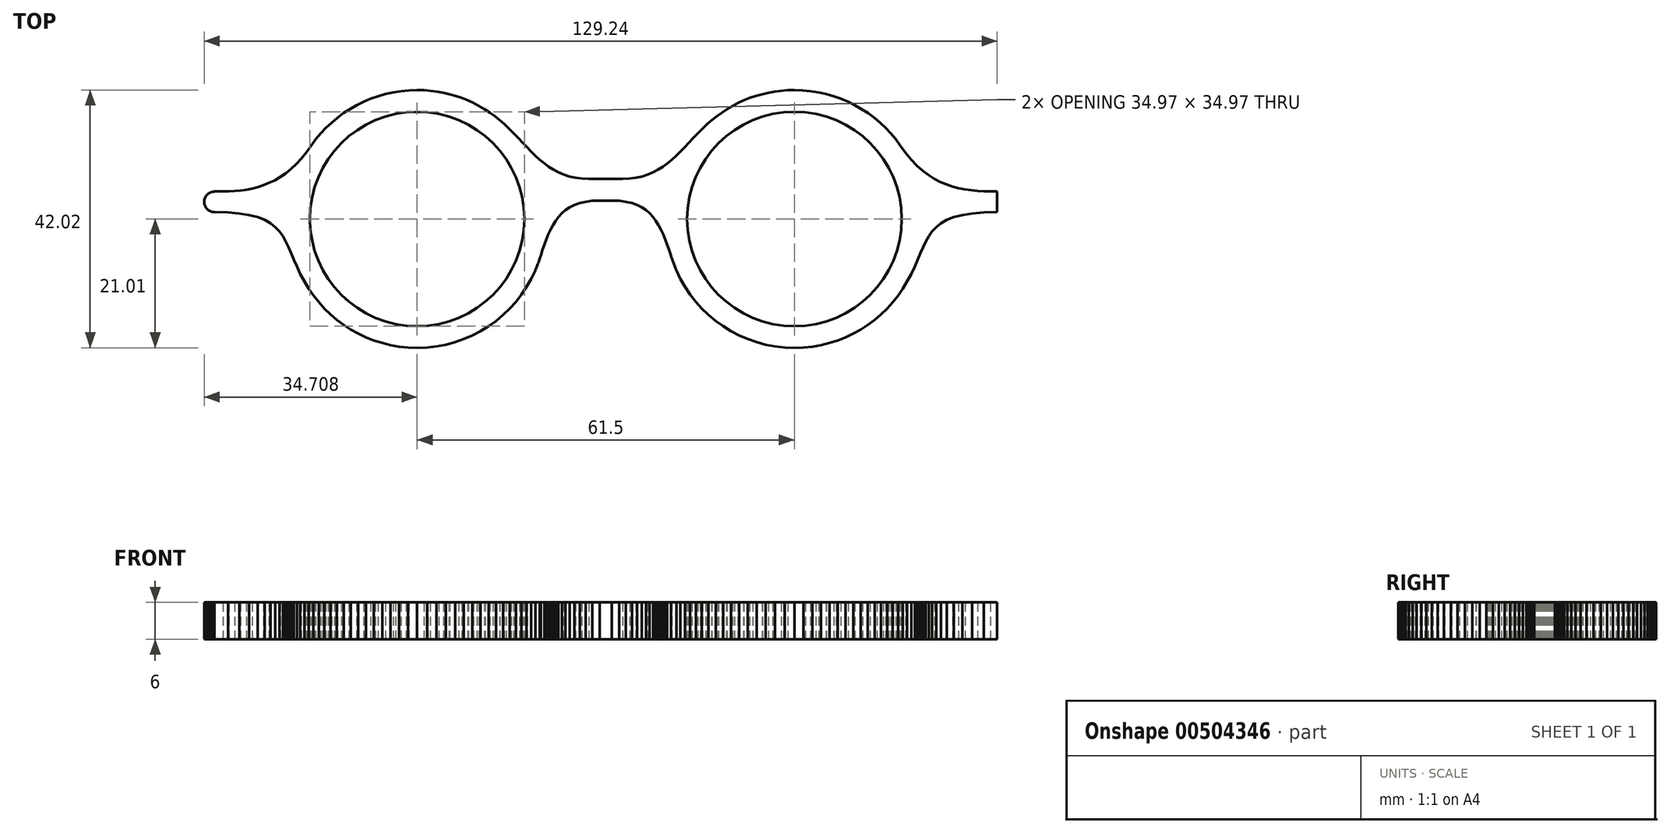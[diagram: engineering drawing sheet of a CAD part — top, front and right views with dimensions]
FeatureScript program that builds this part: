
annotation { "Feature Type Name" : "Feature", "Feature Type Description" : "" }
export const myFeature = defineFeature(function(context is Context, id is Id, definition is map)
    precondition{}
    {
        {
            var Q0;
            Q0=qCreatedBy(makeId("Top.planeOp"),FACE);
            var sketch = newSketch(context, id + "F0", { "sketchPlane" : qUnion([Q0])});
            skLineSegment(sketch, "E0", {"start": v(-47.15, 12) * mm, "end": v(-47.14, 12) * mm});
            skLineSegment(sketch, "E1", {"start": v(-47.14, 12) * mm, "end": v(-47.14, 12.01) * mm});
            skLineSegment(sketch, "E2", {"start": v(-47.14, 12.01) * mm, "end": v(-47.14, 12.01) * mm});
            skLineSegment(sketch, "E3", {"start": v(-47.14, 12.01) * mm, "end": v(-47.14, 12) * mm});
            skLineSegment(sketch, "E4", {"start": v(-47.14, 12) * mm, "end": v(-47.15, 12) * mm});
            skLineSegment(sketch, "E5", {"start": v(-47.15, 12) * mm, "end": v(-47.15, 12) * mm});
            skLineSegment(sketch, "E6", {"start": v(-47.15, 12) * mm, "end": v(-47.16, 12) * mm});
            skLineSegment(sketch, "E7", {"start": v(-47.16, 12) * mm, "end": v(-47.16, 11.99) * mm});
            skLineSegment(sketch, "E8", {"start": v(-47.16, 11.99) * mm, "end": v(-47.16, 11.99) * mm});
            skLineSegment(sketch, "E9", {"start": v(-47.16, 11.99) * mm, "end": v(-47.15, 12) * mm});
            skLineSegment(sketch, "E10", {"start": v(48.83, 11.99) * mm, "end": v(48.83, 12) * mm});
            skLineSegment(sketch, "E11", {"start": v(48.83, 12) * mm, "end": v(48.83, 12) * mm});
            skLineSegment(sketch, "E12", {"start": v(48.83, 12) * mm, "end": v(48.82, 12) * mm});
            skLineSegment(sketch, "E13", {"start": v(48.82, 12) * mm, "end": v(48.82, 12) * mm});
            skLineSegment(sketch, "E14", {"start": v(48.82, 12) * mm, "end": v(48.82, 12.01) * mm});
            skLineSegment(sketch, "E15", {"start": v(48.82, 12.01) * mm, "end": v(48.82, 12.01) * mm});
            skLineSegment(sketch, "E16", {"start": v(48.82, 12.01) * mm, "end": v(48.81, 12.01) * mm});
            skLineSegment(sketch, "E17", {"start": v(48.81, 12.01) * mm, "end": v(48.82, 12.01) * mm});
            skLineSegment(sketch, "E18", {"start": v(48.82, 12.01) * mm, "end": v(48.82, 12) * mm});
            skLineSegment(sketch, "E19", {"start": v(48.82, 12) * mm, "end": v(48.83, 12) * mm});
            skLineSegment(sketch, "E20", {"start": v(48.83, 12) * mm, "end": v(48.83, 11.99) * mm});
            skLineSegment(sketch, "E21", {"start": v(48.83, 11.99) * mm, "end": v(48.83, 11.99) * mm});
            skLineSegment(sketch, "E22", {"start": v(63.55, 4.48) * mm, "end": v(62.5, 4.5) * mm});
            skLineSegment(sketch, "E23", {"start": v(62.5, 4.5) * mm, "end": v(61.45, 4.57) * mm});
            skLineSegment(sketch, "E24", {"start": v(61.45, 4.57) * mm, "end": v(60.41, 4.67) * mm});
            skLineSegment(sketch, "E25", {"start": v(60.41, 4.67) * mm, "end": v(59.38, 4.82) * mm});
            skLineSegment(sketch, "E26", {"start": v(59.38, 4.82) * mm, "end": v(58.36, 5.02) * mm});
            skLineSegment(sketch, "E27", {"start": v(58.36, 5.02) * mm, "end": v(57.35, 5.29) * mm});
            skLineSegment(sketch, "E28", {"start": v(57.35, 5.29) * mm, "end": v(56.35, 5.62) * mm});
            skLineSegment(sketch, "E29", {"start": v(56.35, 5.62) * mm, "end": v(55.36, 6.05) * mm});
            skLineSegment(sketch, "E30", {"start": v(55.36, 6.05) * mm, "end": v(54.38, 6.56) * mm});
            skLineSegment(sketch, "E31", {"start": v(54.38, 6.56) * mm, "end": v(53.42, 7.17) * mm});
            skLineSegment(sketch, "E32", {"start": v(53.42, 7.17) * mm, "end": v(52.47, 7.88) * mm});
            skLineSegment(sketch, "E33", {"start": v(52.47, 7.88) * mm, "end": v(51.54, 8.71) * mm});
            skLineSegment(sketch, "E34", {"start": v(51.54, 8.71) * mm, "end": v(50.62, 9.67) * mm});
            skLineSegment(sketch, "E35", {"start": v(50.62, 9.67) * mm, "end": v(49.72, 10.76) * mm});
            skLineSegment(sketch, "E36", {"start": v(49.72, 10.76) * mm, "end": v(48.83, 11.99) * mm});
            skLineSegment(sketch, "E37", {"start": v(48.83, 11.99) * mm, "end": v(48.1, 12.99) * mm});
            skLineSegment(sketch, "E38", {"start": v(48.1, 12.99) * mm, "end": v(47.3, 13.94) * mm});
            skLineSegment(sketch, "E39", {"start": v(47.3, 13.94) * mm, "end": v(46.44, 14.84) * mm});
            skLineSegment(sketch, "E40", {"start": v(46.44, 14.84) * mm, "end": v(45.54, 15.7) * mm});
            skLineSegment(sketch, "E41", {"start": v(45.54, 15.7) * mm, "end": v(44.59, 16.5) * mm});
            skLineSegment(sketch, "E42", {"start": v(44.59, 16.5) * mm, "end": v(43.59, 17.24) * mm});
            skLineSegment(sketch, "E43", {"start": v(43.59, 17.24) * mm, "end": v(42.54, 17.92) * mm});
            skLineSegment(sketch, "E44", {"start": v(42.54, 17.92) * mm, "end": v(41.46, 18.54) * mm});
            skLineSegment(sketch, "E45", {"start": v(41.46, 18.54) * mm, "end": v(40.34, 19.1) * mm});
            skLineSegment(sketch, "E46", {"start": v(40.34, 19.1) * mm, "end": v(39.18, 19.6) * mm});
            skLineSegment(sketch, "E47", {"start": v(39.18, 19.6) * mm, "end": v(37.98, 20.02) * mm});
            skLineSegment(sketch, "E48", {"start": v(37.98, 20.02) * mm, "end": v(36.76, 20.37) * mm});
            skLineSegment(sketch, "E49", {"start": v(36.76, 20.37) * mm, "end": v(35.5, 20.65) * mm});
            skLineSegment(sketch, "E50", {"start": v(35.5, 20.65) * mm, "end": v(34.22, 20.85) * mm});
            skLineSegment(sketch, "E51", {"start": v(34.22, 20.85) * mm, "end": v(32.92, 20.97) * mm});
            skLineSegment(sketch, "E52", {"start": v(32.92, 20.97) * mm, "end": v(31.59, 21.01) * mm});
            skLineSegment(sketch, "E53", {"start": v(31.59, 21.01) * mm, "end": v(30.5, 20.99) * mm});
            skLineSegment(sketch, "E54", {"start": v(30.5, 20.99) * mm, "end": v(29.42, 20.9) * mm});
            skLineSegment(sketch, "E55", {"start": v(29.42, 20.9) * mm, "end": v(28.36, 20.77) * mm});
            skLineSegment(sketch, "E56", {"start": v(28.36, 20.77) * mm, "end": v(27.32, 20.58) * mm});
            skLineSegment(sketch, "E57", {"start": v(27.32, 20.58) * mm, "end": v(26.3, 20.34) * mm});
            skLineSegment(sketch, "E58", {"start": v(26.3, 20.34) * mm, "end": v(25.3, 20.05) * mm});
            skLineSegment(sketch, "E59", {"start": v(25.3, 20.05) * mm, "end": v(24.31, 19.71) * mm});
            skLineSegment(sketch, "E60", {"start": v(24.31, 19.71) * mm, "end": v(23.35, 19.33) * mm});
            skLineSegment(sketch, "E61", {"start": v(23.35, 19.33) * mm, "end": v(22.41, 18.9) * mm});
            skLineSegment(sketch, "E62", {"start": v(22.41, 18.9) * mm, "end": v(21.5, 18.43) * mm});
            skLineSegment(sketch, "E63", {"start": v(21.5, 18.43) * mm, "end": v(20.62, 17.91) * mm});
            skLineSegment(sketch, "E64", {"start": v(20.62, 17.91) * mm, "end": v(19.76, 17.36) * mm});
            skLineSegment(sketch, "E65", {"start": v(19.76, 17.36) * mm, "end": v(18.93, 16.76) * mm});
            skLineSegment(sketch, "E66", {"start": v(18.93, 16.76) * mm, "end": v(18.13, 16.13) * mm});
            skLineSegment(sketch, "E67", {"start": v(18.13, 16.13) * mm, "end": v(17.37, 15.46) * mm});
            skLineSegment(sketch, "E68", {"start": v(17.37, 15.46) * mm, "end": v(16.63, 14.75) * mm});
            skLineSegment(sketch, "E69", {"start": v(16.63, 14.75) * mm, "end": v(15.85, 13.97) * mm});
            skLineSegment(sketch, "E70", {"start": v(15.85, 13.97) * mm, "end": v(15.1, 13.2) * mm});
            skLineSegment(sketch, "E71", {"start": v(15.1, 13.2) * mm, "end": v(14.38, 12.44) * mm});
            skLineSegment(sketch, "E72", {"start": v(14.38, 12.44) * mm, "end": v(13.67, 11.7) * mm});
            skLineSegment(sketch, "E73", {"start": v(13.67, 11.7) * mm, "end": v(12.97, 10.99) * mm});
            skLineSegment(sketch, "E74", {"start": v(12.97, 10.99) * mm, "end": v(12.28, 10.3) * mm});
            skLineSegment(sketch, "E75", {"start": v(12.28, 10.3) * mm, "end": v(11.58, 9.67) * mm});
            skLineSegment(sketch, "E76", {"start": v(11.58, 9.67) * mm, "end": v(10.86, 9.07) * mm});
            skLineSegment(sketch, "E77", {"start": v(10.86, 9.07) * mm, "end": v(10.12, 8.52) * mm});
            skLineSegment(sketch, "E78", {"start": v(10.12, 8.52) * mm, "end": v(9.35, 8.03) * mm});
            skLineSegment(sketch, "E79", {"start": v(9.35, 8.03) * mm, "end": v(8.54, 7.6) * mm});
            skLineSegment(sketch, "E80", {"start": v(8.54, 7.6) * mm, "end": v(7.68, 7.23) * mm});
            skLineSegment(sketch, "E81", {"start": v(7.68, 7.23) * mm, "end": v(6.77, 6.93) * mm});
            skLineSegment(sketch, "E82", {"start": v(6.77, 6.93) * mm, "end": v(5.78, 6.71) * mm});
            skLineSegment(sketch, "E83", {"start": v(5.78, 6.71) * mm, "end": v(4.73, 6.58) * mm});
            skLineSegment(sketch, "E84", {"start": v(4.73, 6.58) * mm, "end": v(3.6, 6.53) * mm});
            skLineSegment(sketch, "E85", {"start": v(3.6, 6.53) * mm, "end": v(3.25, 6.53) * mm});
            skLineSegment(sketch, "E86", {"start": v(3.25, 6.53) * mm, "end": v(2.9, 6.53) * mm});
            skLineSegment(sketch, "E87", {"start": v(2.9, 6.53) * mm, "end": v(2.56, 6.53) * mm});
            skLineSegment(sketch, "E88", {"start": v(2.56, 6.53) * mm, "end": v(2.21, 6.53) * mm});
            skLineSegment(sketch, "E89", {"start": v(2.21, 6.53) * mm, "end": v(1.87, 6.53) * mm});
            skLineSegment(sketch, "E90", {"start": v(1.87, 6.53) * mm, "end": v(1.53, 6.53) * mm});
            skLineSegment(sketch, "E91", {"start": v(1.53, 6.53) * mm, "end": v(1.18, 6.53) * mm});
            skLineSegment(sketch, "E92", {"start": v(1.18, 6.53) * mm, "end": v(0.84, 6.53) * mm});
            skLineSegment(sketch, "E93", {"start": v(0.84, 6.53) * mm, "end": v(0.5, 6.53) * mm});
            skLineSegment(sketch, "E94", {"start": v(0.5, 6.53) * mm, "end": v(0.15, 6.53) * mm});
            skLineSegment(sketch, "E95", {"start": v(0.15, 6.53) * mm, "end": v(-0.2, 6.53) * mm});
            skLineSegment(sketch, "E96", {"start": v(-0.2, 6.53) * mm, "end": v(-0.54, 6.53) * mm});
            skLineSegment(sketch, "E97", {"start": v(-0.54, 6.53) * mm, "end": v(-0.88, 6.53) * mm});
            skLineSegment(sketch, "E98", {"start": v(-0.88, 6.53) * mm, "end": v(-1.23, 6.53) * mm});
            skLineSegment(sketch, "E99", {"start": v(-1.23, 6.53) * mm, "end": v(-1.57, 6.53) * mm});
            skLineSegment(sketch, "E100", {"start": v(-1.57, 6.53) * mm, "end": v(-1.92, 6.53) * mm});
            skLineSegment(sketch, "E101", {"start": v(-1.92, 6.53) * mm, "end": v(-3.05, 6.58) * mm});
            skLineSegment(sketch, "E102", {"start": v(-3.05, 6.58) * mm, "end": v(-4.1, 6.71) * mm});
            skLineSegment(sketch, "E103", {"start": v(-4.1, 6.71) * mm, "end": v(-5.1, 6.93) * mm});
            skLineSegment(sketch, "E104", {"start": v(-5.1, 6.93) * mm, "end": v(-6, 7.23) * mm});
            skLineSegment(sketch, "E105", {"start": v(-6, 7.23) * mm, "end": v(-6.87, 7.6) * mm});
            skLineSegment(sketch, "E106", {"start": v(-6.87, 7.6) * mm, "end": v(-7.68, 8.03) * mm});
            skLineSegment(sketch, "E107", {"start": v(-7.68, 8.03) * mm, "end": v(-8.45, 8.52) * mm});
            skLineSegment(sketch, "E108", {"start": v(-8.45, 8.52) * mm, "end": v(-9.19, 9.07) * mm});
            skLineSegment(sketch, "E109", {"start": v(-9.19, 9.07) * mm, "end": v(-9.9, 9.67) * mm});
            skLineSegment(sketch, "E110", {"start": v(-9.9, 9.67) * mm, "end": v(-10.6, 10.3) * mm});
            skLineSegment(sketch, "E111", {"start": v(-10.6, 10.3) * mm, "end": v(-11.3, 10.99) * mm});
            skLineSegment(sketch, "E112", {"start": v(-11.3, 10.99) * mm, "end": v(-12, 11.7) * mm});
            skLineSegment(sketch, "E113", {"start": v(-12, 11.7) * mm, "end": v(-12.7, 12.44) * mm});
            skLineSegment(sketch, "E114", {"start": v(-12.7, 12.44) * mm, "end": v(-13.42, 13.2) * mm});
            skLineSegment(sketch, "E115", {"start": v(-13.42, 13.2) * mm, "end": v(-14.17, 13.97) * mm});
            skLineSegment(sketch, "E116", {"start": v(-14.17, 13.97) * mm, "end": v(-14.96, 14.75) * mm});
            skLineSegment(sketch, "E117", {"start": v(-14.96, 14.75) * mm, "end": v(-15.7, 15.46) * mm});
            skLineSegment(sketch, "E118", {"start": v(-15.7, 15.46) * mm, "end": v(-16.46, 16.13) * mm});
            skLineSegment(sketch, "E119", {"start": v(-16.46, 16.13) * mm, "end": v(-17.26, 16.76) * mm});
            skLineSegment(sketch, "E120", {"start": v(-17.26, 16.76) * mm, "end": v(-18.08, 17.36) * mm});
            skLineSegment(sketch, "E121", {"start": v(-18.08, 17.36) * mm, "end": v(-18.94, 17.91) * mm});
            skLineSegment(sketch, "E122", {"start": v(-18.94, 17.91) * mm, "end": v(-19.83, 18.43) * mm});
            skLineSegment(sketch, "E123", {"start": v(-19.83, 18.43) * mm, "end": v(-20.74, 18.9) * mm});
            skLineSegment(sketch, "E124", {"start": v(-20.74, 18.9) * mm, "end": v(-21.67, 19.33) * mm});
            skLineSegment(sketch, "E125", {"start": v(-21.67, 19.33) * mm, "end": v(-22.64, 19.71) * mm});
            skLineSegment(sketch, "E126", {"start": v(-22.64, 19.71) * mm, "end": v(-23.62, 20.05) * mm});
            skLineSegment(sketch, "E127", {"start": v(-23.62, 20.05) * mm, "end": v(-24.62, 20.34) * mm});
            skLineSegment(sketch, "E128", {"start": v(-24.62, 20.34) * mm, "end": v(-25.65, 20.58) * mm});
            skLineSegment(sketch, "E129", {"start": v(-25.65, 20.58) * mm, "end": v(-26.69, 20.77) * mm});
            skLineSegment(sketch, "E130", {"start": v(-26.69, 20.77) * mm, "end": v(-27.75, 20.9) * mm});
            skLineSegment(sketch, "E131", {"start": v(-27.75, 20.9) * mm, "end": v(-28.82, 20.99) * mm});
            skLineSegment(sketch, "E132", {"start": v(-28.82, 20.99) * mm, "end": v(-29.91, 21.01) * mm});
            skLineSegment(sketch, "E133", {"start": v(-29.91, 21.01) * mm, "end": v(-31.24, 20.97) * mm});
            skLineSegment(sketch, "E134", {"start": v(-31.24, 20.97) * mm, "end": v(-32.55, 20.85) * mm});
            skLineSegment(sketch, "E135", {"start": v(-32.55, 20.85) * mm, "end": v(-33.83, 20.65) * mm});
            skLineSegment(sketch, "E136", {"start": v(-33.83, 20.65) * mm, "end": v(-35.08, 20.37) * mm});
            skLineSegment(sketch, "E137", {"start": v(-35.08, 20.37) * mm, "end": v(-36.3, 20.02) * mm});
            skLineSegment(sketch, "E138", {"start": v(-36.3, 20.02) * mm, "end": v(-37.5, 19.6) * mm});
            skLineSegment(sketch, "E139", {"start": v(-37.5, 19.6) * mm, "end": v(-38.66, 19.1) * mm});
            skLineSegment(sketch, "E140", {"start": v(-38.66, 19.1) * mm, "end": v(-39.78, 18.54) * mm});
            skLineSegment(sketch, "E141", {"start": v(-39.78, 18.54) * mm, "end": v(-40.87, 17.92) * mm});
            skLineSegment(sketch, "E142", {"start": v(-40.87, 17.92) * mm, "end": v(-41.91, 17.24) * mm});
            skLineSegment(sketch, "E143", {"start": v(-41.91, 17.24) * mm, "end": v(-42.91, 16.5) * mm});
            skLineSegment(sketch, "E144", {"start": v(-42.91, 16.5) * mm, "end": v(-43.86, 15.7) * mm});
            skLineSegment(sketch, "E145", {"start": v(-43.86, 15.7) * mm, "end": v(-44.77, 14.84) * mm});
            skLineSegment(sketch, "E146", {"start": v(-44.77, 14.84) * mm, "end": v(-45.62, 13.94) * mm});
            skLineSegment(sketch, "E147", {"start": v(-45.62, 13.94) * mm, "end": v(-46.42, 12.99) * mm});
            skLineSegment(sketch, "E148", {"start": v(-46.42, 12.99) * mm, "end": v(-47.16, 11.99) * mm});
            skLineSegment(sketch, "E149", {"start": v(-47.16, 11.99) * mm, "end": v(-47.97, 10.85) * mm});
            skLineSegment(sketch, "E150", {"start": v(-47.97, 10.85) * mm, "end": v(-48.8, 9.84) * mm});
            skLineSegment(sketch, "E151", {"start": v(-48.8, 9.84) * mm, "end": v(-49.64, 8.93) * mm});
            skLineSegment(sketch, "E152", {"start": v(-49.64, 8.93) * mm, "end": v(-50.5, 8.14) * mm});
            skLineSegment(sketch, "E153", {"start": v(-50.5, 8.14) * mm, "end": v(-51.36, 7.44) * mm});
            skLineSegment(sketch, "E154", {"start": v(-51.36, 7.44) * mm, "end": v(-52.24, 6.83) * mm});
            skLineSegment(sketch, "E155", {"start": v(-52.24, 6.83) * mm, "end": v(-53.13, 6.31) * mm});
            skLineSegment(sketch, "E156", {"start": v(-53.13, 6.31) * mm, "end": v(-54.03, 5.87) * mm});
            skLineSegment(sketch, "E157", {"start": v(-54.03, 5.87) * mm, "end": v(-54.95, 5.5) * mm});
            skLineSegment(sketch, "E158", {"start": v(-54.95, 5.5) * mm, "end": v(-55.87, 5.2) * mm});
            skLineSegment(sketch, "E159", {"start": v(-55.87, 5.2) * mm, "end": v(-56.8, 4.97) * mm});
            skLineSegment(sketch, "E160", {"start": v(-56.8, 4.97) * mm, "end": v(-57.73, 4.79) * mm});
            skLineSegment(sketch, "E161", {"start": v(-57.73, 4.79) * mm, "end": v(-58.68, 4.65) * mm});
            skLineSegment(sketch, "E162", {"start": v(-58.68, 4.65) * mm, "end": v(-59.63, 4.56) * mm});
            skLineSegment(sketch, "E163", {"start": v(-59.63, 4.56) * mm, "end": v(-60.58, 4.5) * mm});
            skLineSegment(sketch, "E164", {"start": v(-60.58, 4.5) * mm, "end": v(-61.54, 4.48) * mm});
            skLineSegment(sketch, "E165", {"start": v(-61.54, 4.48) * mm, "end": v(-61.63, 4.48) * mm});
            skLineSegment(sketch, "E166", {"start": v(-61.63, 4.48) * mm, "end": v(-61.72, 4.48) * mm});
            skLineSegment(sketch, "E167", {"start": v(-61.72, 4.48) * mm, "end": v(-61.8, 4.48) * mm});
            skLineSegment(sketch, "E168", {"start": v(-61.8, 4.48) * mm, "end": v(-61.9, 4.48) * mm});
            skLineSegment(sketch, "E169", {"start": v(-61.9, 4.48) * mm, "end": v(-61.98, 4.48) * mm});
            skLineSegment(sketch, "E170", {"start": v(-61.98, 4.48) * mm, "end": v(-62.07, 4.48) * mm});
            skLineSegment(sketch, "E171", {"start": v(-62.07, 4.48) * mm, "end": v(-62.16, 4.48) * mm});
            skLineSegment(sketch, "E172", {"start": v(-62.16, 4.48) * mm, "end": v(-62.24, 4.47) * mm});
            skLineSegment(sketch, "E173", {"start": v(-62.24, 4.47) * mm, "end": v(-62.33, 4.47) * mm});
            skLineSegment(sketch, "E174", {"start": v(-62.33, 4.47) * mm, "end": v(-62.42, 4.47) * mm});
            skLineSegment(sketch, "E175", {"start": v(-62.42, 4.47) * mm, "end": v(-62.5, 4.47) * mm});
            skLineSegment(sketch, "E176", {"start": v(-62.5, 4.47) * mm, "end": v(-62.6, 4.47) * mm});
            skLineSegment(sketch, "E177", {"start": v(-62.6, 4.47) * mm, "end": v(-62.68, 4.47) * mm});
            skLineSegment(sketch, "E178", {"start": v(-62.68, 4.47) * mm, "end": v(-62.77, 4.47) * mm});
            skLineSegment(sketch, "E179", {"start": v(-62.77, 4.47) * mm, "end": v(-62.85, 4.47) * mm});
            skLineSegment(sketch, "E180", {"start": v(-62.85, 4.47) * mm, "end": v(-62.94, 4.47) * mm});
            skLineSegment(sketch, "E181", {"start": v(-62.94, 4.47) * mm, "end": v(-62.94, 4.47) * mm});
            skLineSegment(sketch, "E182", {"start": v(-62.94, 4.47) * mm, "end": v(-63.11, 4.46) * mm});
            skLineSegment(sketch, "E183", {"start": v(-63.11, 4.46) * mm, "end": v(-63.28, 4.44) * mm});
            skLineSegment(sketch, "E184", {"start": v(-63.28, 4.44) * mm, "end": v(-63.44, 4.4) * mm});
            skLineSegment(sketch, "E185", {"start": v(-63.44, 4.4) * mm, "end": v(-63.6, 4.34) * mm});
            skLineSegment(sketch, "E186", {"start": v(-63.6, 4.34) * mm, "end": v(-63.74, 4.27) * mm});
            skLineSegment(sketch, "E187", {"start": v(-63.74, 4.27) * mm, "end": v(-63.88, 4.18) * mm});
            skLineSegment(sketch, "E188", {"start": v(-63.88, 4.18) * mm, "end": v(-64, 4.09) * mm});
            skLineSegment(sketch, "E189", {"start": v(-64, 4.09) * mm, "end": v(-64.12, 3.98) * mm});
            skLineSegment(sketch, "E190", {"start": v(-64.12, 3.98) * mm, "end": v(-64.23, 3.86) * mm});
            skLineSegment(sketch, "E191", {"start": v(-64.23, 3.86) * mm, "end": v(-64.33, 3.73) * mm});
            skLineSegment(sketch, "E192", {"start": v(-64.33, 3.73) * mm, "end": v(-64.41, 3.6) * mm});
            skLineSegment(sketch, "E193", {"start": v(-64.41, 3.6) * mm, "end": v(-64.48, 3.45) * mm});
            skLineSegment(sketch, "E194", {"start": v(-64.48, 3.45) * mm, "end": v(-64.54, 3.3) * mm});
            skLineSegment(sketch, "E195", {"start": v(-64.54, 3.3) * mm, "end": v(-64.58, 3.13) * mm});
            skLineSegment(sketch, "E196", {"start": v(-64.58, 3.13) * mm, "end": v(-64.6, 2.97) * mm});
            skLineSegment(sketch, "E197", {"start": v(-64.6, 2.97) * mm, "end": v(-64.62, 2.8) * mm});
            skLineSegment(sketch, "E198", {"start": v(-64.62, 2.8) * mm, "end": v(-64.6, 2.62) * mm});
            skLineSegment(sketch, "E199", {"start": v(-64.6, 2.62) * mm, "end": v(-64.58, 2.46) * mm});
            skLineSegment(sketch, "E200", {"start": v(-64.58, 2.46) * mm, "end": v(-64.54, 2.3) * mm});
            skLineSegment(sketch, "E201", {"start": v(-64.54, 2.3) * mm, "end": v(-64.48, 2.14) * mm});
            skLineSegment(sketch, "E202", {"start": v(-64.48, 2.14) * mm, "end": v(-64.41, 2) * mm});
            skLineSegment(sketch, "E203", {"start": v(-64.41, 2) * mm, "end": v(-64.33, 1.86) * mm});
            skLineSegment(sketch, "E204", {"start": v(-64.33, 1.86) * mm, "end": v(-64.23, 1.73) * mm});
            skLineSegment(sketch, "E205", {"start": v(-64.23, 1.73) * mm, "end": v(-64.12, 1.6) * mm});
            skLineSegment(sketch, "E206", {"start": v(-64.12, 1.6) * mm, "end": v(-64, 1.5) * mm});
            skLineSegment(sketch, "E207", {"start": v(-64, 1.5) * mm, "end": v(-63.88, 1.4) * mm});
            skLineSegment(sketch, "E208", {"start": v(-63.88, 1.4) * mm, "end": v(-63.74, 1.32) * mm});
            skLineSegment(sketch, "E209", {"start": v(-63.74, 1.32) * mm, "end": v(-63.6, 1.25) * mm});
            skLineSegment(sketch, "E210", {"start": v(-63.6, 1.25) * mm, "end": v(-63.44, 1.2) * mm});
            skLineSegment(sketch, "E211", {"start": v(-63.44, 1.2) * mm, "end": v(-63.28, 1.15) * mm});
            skLineSegment(sketch, "E212", {"start": v(-63.28, 1.15) * mm, "end": v(-63.11, 1.13) * mm});
            skLineSegment(sketch, "E213", {"start": v(-63.11, 1.13) * mm, "end": v(-62.94, 1.12) * mm});
            skLineSegment(sketch, "E214", {"start": v(-62.94, 1.12) * mm, "end": v(-62.94, 1.12) * mm});
            skLineSegment(sketch, "E215", {"start": v(-62.94, 1.12) * mm, "end": v(-60.76, 1.06) * mm});
            skLineSegment(sketch, "E216", {"start": v(-60.76, 1.06) * mm, "end": v(-58.88, 0.9) * mm});
            skLineSegment(sketch, "E217", {"start": v(-58.88, 0.9) * mm, "end": v(-57.28, 0.65) * mm});
            skLineSegment(sketch, "E218", {"start": v(-57.28, 0.65) * mm, "end": v(-55.92, 0.29) * mm});
            skLineSegment(sketch, "E219", {"start": v(-55.92, 0.29) * mm, "end": v(-54.78, -0.16) * mm});
            skLineSegment(sketch, "E220", {"start": v(-54.78, -0.16) * mm, "end": v(-53.82, -0.7) * mm});
            skLineSegment(sketch, "E221", {"start": v(-53.82, -0.7) * mm, "end": v(-53.03, -1.33) * mm});
            skLineSegment(sketch, "E222", {"start": v(-53.03, -1.33) * mm, "end": v(-52.37, -2.04) * mm});
            skLineSegment(sketch, "E223", {"start": v(-52.37, -2.04) * mm, "end": v(-51.8, -2.82) * mm});
            skLineSegment(sketch, "E224", {"start": v(-51.8, -2.82) * mm, "end": v(-51.32, -3.68) * mm});
            skLineSegment(sketch, "E225", {"start": v(-51.32, -3.68) * mm, "end": v(-50.88, -4.6) * mm});
            skLineSegment(sketch, "E226", {"start": v(-50.88, -4.6) * mm, "end": v(-50.45, -5.6) * mm});
            skLineSegment(sketch, "E227", {"start": v(-50.45, -5.6) * mm, "end": v(-50, -6.66) * mm});
            skLineSegment(sketch, "E228", {"start": v(-50, -6.66) * mm, "end": v(-49.52, -7.77) * mm});
            skLineSegment(sketch, "E229", {"start": v(-49.52, -7.77) * mm, "end": v(-48.96, -8.94) * mm});
            skLineSegment(sketch, "E230", {"start": v(-48.96, -8.94) * mm, "end": v(-48.3, -10.15) * mm});
            skLineSegment(sketch, "E231", {"start": v(-48.3, -10.15) * mm, "end": v(-47.6, -11.34) * mm});
            skLineSegment(sketch, "E232", {"start": v(-47.6, -11.34) * mm, "end": v(-46.8, -12.48) * mm});
            skLineSegment(sketch, "E233", {"start": v(-46.8, -12.48) * mm, "end": v(-45.95, -13.56) * mm});
            skLineSegment(sketch, "E234", {"start": v(-45.95, -13.56) * mm, "end": v(-45.03, -14.58) * mm});
            skLineSegment(sketch, "E235", {"start": v(-45.03, -14.58) * mm, "end": v(-44.04, -15.54) * mm});
            skLineSegment(sketch, "E236", {"start": v(-44.04, -15.54) * mm, "end": v(-43, -16.43) * mm});
            skLineSegment(sketch, "E237", {"start": v(-43, -16.43) * mm, "end": v(-41.89, -17.26) * mm});
            skLineSegment(sketch, "E238", {"start": v(-41.89, -17.26) * mm, "end": v(-40.73, -18) * mm});
            skLineSegment(sketch, "E239", {"start": v(-40.73, -18) * mm, "end": v(-39.52, -18.69) * mm});
            skLineSegment(sketch, "E240", {"start": v(-39.52, -18.69) * mm, "end": v(-38.26, -19.28) * mm});
            skLineSegment(sketch, "E241", {"start": v(-38.26, -19.28) * mm, "end": v(-36.96, -19.8) * mm});
            skLineSegment(sketch, "E242", {"start": v(-36.96, -19.8) * mm, "end": v(-35.62, -20.23) * mm});
            skLineSegment(sketch, "E243", {"start": v(-35.62, -20.23) * mm, "end": v(-34.24, -20.57) * mm});
            skLineSegment(sketch, "E244", {"start": v(-34.24, -20.57) * mm, "end": v(-32.83, -20.81) * mm});
            skLineSegment(sketch, "E245", {"start": v(-32.83, -20.81) * mm, "end": v(-31.38, -20.96) * mm});
            skLineSegment(sketch, "E246", {"start": v(-31.38, -20.96) * mm, "end": v(-29.91, -21.01) * mm});
            skLineSegment(sketch, "E247", {"start": v(-29.91, -21.01) * mm, "end": v(-28.31, -20.95) * mm});
            skLineSegment(sketch, "E248", {"start": v(-28.31, -20.95) * mm, "end": v(-26.75, -20.78) * mm});
            skLineSegment(sketch, "E249", {"start": v(-26.75, -20.78) * mm, "end": v(-25.22, -20.49) * mm});
            skLineSegment(sketch, "E250", {"start": v(-25.22, -20.49) * mm, "end": v(-23.73, -20.09) * mm});
            skLineSegment(sketch, "E251", {"start": v(-23.73, -20.09) * mm, "end": v(-22.3, -19.58) * mm});
            skLineSegment(sketch, "E252", {"start": v(-22.3, -19.58) * mm, "end": v(-20.9, -18.98) * mm});
            skLineSegment(sketch, "E253", {"start": v(-20.9, -18.98) * mm, "end": v(-19.56, -18.28) * mm});
            skLineSegment(sketch, "E254", {"start": v(-19.56, -18.28) * mm, "end": v(-18.28, -17.5) * mm});
            skLineSegment(sketch, "E255", {"start": v(-18.28, -17.5) * mm, "end": v(-17.06, -16.61) * mm});
            skLineSegment(sketch, "E256", {"start": v(-17.06, -16.61) * mm, "end": v(-15.91, -15.65) * mm});
            skLineSegment(sketch, "E257", {"start": v(-15.91, -15.65) * mm, "end": v(-14.83, -14.62) * mm});
            skLineSegment(sketch, "E258", {"start": v(-14.83, -14.62) * mm, "end": v(-13.83, -13.5) * mm});
            skLineSegment(sketch, "E259", {"start": v(-13.83, -13.5) * mm, "end": v(-12.9, -12.32) * mm});
            skLineSegment(sketch, "E260", {"start": v(-12.9, -12.32) * mm, "end": v(-12.07, -11.08) * mm});
            skLineSegment(sketch, "E261", {"start": v(-12.07, -11.08) * mm, "end": v(-11.32, -9.77) * mm});
            skLineSegment(sketch, "E262", {"start": v(-11.32, -9.77) * mm, "end": v(-10.66, -8.4) * mm});
            skLineSegment(sketch, "E263", {"start": v(-10.66, -8.4) * mm, "end": v(-10.65, -8.4) * mm});
            skLineSegment(sketch, "E264", {"start": v(-10.65, -8.4) * mm, "end": v(-10.63, -8.34) * mm});
            skLineSegment(sketch, "E265", {"start": v(-10.63, -8.34) * mm, "end": v(-10.6, -8.25) * mm});
            skLineSegment(sketch, "E266", {"start": v(-10.6, -8.25) * mm, "end": v(-10.55, -8.14) * mm});
            skLineSegment(sketch, "E267", {"start": v(-10.55, -8.14) * mm, "end": v(-10.5, -8) * mm});
            skLineSegment(sketch, "E268", {"start": v(-10.5, -8) * mm, "end": v(-10.44, -7.85) * mm});
            skLineSegment(sketch, "E269", {"start": v(-10.44, -7.85) * mm, "end": v(-10.37, -7.68) * mm});
            skLineSegment(sketch, "E270", {"start": v(-10.37, -7.68) * mm, "end": v(-10.3, -7.5) * mm});
            skLineSegment(sketch, "E271", {"start": v(-10.3, -7.5) * mm, "end": v(-10.23, -7.3) * mm});
            skLineSegment(sketch, "E272", {"start": v(-10.23, -7.3) * mm, "end": v(-10.15, -7.1) * mm});
            skLineSegment(sketch, "E273", {"start": v(-10.15, -7.1) * mm, "end": v(-10.08, -6.89) * mm});
            skLineSegment(sketch, "E274", {"start": v(-10.08, -6.89) * mm, "end": v(-10, -6.68) * mm});
            skLineSegment(sketch, "E275", {"start": v(-10, -6.68) * mm, "end": v(-9.94, -6.49) * mm});
            skLineSegment(sketch, "E276", {"start": v(-9.94, -6.49) * mm, "end": v(-9.87, -6.3) * mm});
            skLineSegment(sketch, "E277", {"start": v(-9.87, -6.3) * mm, "end": v(-9.81, -6.12) * mm});
            skLineSegment(sketch, "E278", {"start": v(-9.81, -6.12) * mm, "end": v(-9.76, -5.95) * mm});
            skLineSegment(sketch, "E279", {"start": v(-9.76, -5.95) * mm, "end": v(-9.46, -5.05) * mm});
            skLineSegment(sketch, "E280", {"start": v(-9.46, -5.05) * mm, "end": v(-9.15, -4.18) * mm});
            skLineSegment(sketch, "E281", {"start": v(-9.15, -4.18) * mm, "end": v(-8.84, -3.33) * mm});
            skLineSegment(sketch, "E282", {"start": v(-8.84, -3.33) * mm, "end": v(-8.51, -2.51) * mm});
            skLineSegment(sketch, "E283", {"start": v(-8.51, -2.51) * mm, "end": v(-8.16, -1.73) * mm});
            skLineSegment(sketch, "E284", {"start": v(-8.16, -1.73) * mm, "end": v(-7.77, -1) * mm});
            skLineSegment(sketch, "E285", {"start": v(-7.77, -1) * mm, "end": v(-7.35, -0.3) * mm});
            skLineSegment(sketch, "E286", {"start": v(-7.35, -0.3) * mm, "end": v(-6.87, 0.34) * mm});
            skLineSegment(sketch, "E287", {"start": v(-6.87, 0.34) * mm, "end": v(-6.33, 0.93) * mm});
            skLineSegment(sketch, "E288", {"start": v(-6.33, 0.93) * mm, "end": v(-5.73, 1.45) * mm});
            skLineSegment(sketch, "E289", {"start": v(-5.73, 1.45) * mm, "end": v(-5.04, 1.9) * mm});
            skLineSegment(sketch, "E290", {"start": v(-5.04, 1.9) * mm, "end": v(-4.28, 2.29) * mm});
            skLineSegment(sketch, "E291", {"start": v(-4.28, 2.29) * mm, "end": v(-3.41, 2.6) * mm});
            skLineSegment(sketch, "E292", {"start": v(-3.41, 2.6) * mm, "end": v(-2.44, 2.82) * mm});
            skLineSegment(sketch, "E293", {"start": v(-2.44, 2.82) * mm, "end": v(-1.36, 2.96) * mm});
            skLineSegment(sketch, "E294", {"start": v(-1.36, 2.96) * mm, "end": v(-0.16, 3) * mm});
            skLineSegment(sketch, "E295", {"start": v(-0.16, 3) * mm, "end": v(-0.04, 3) * mm});
            skLineSegment(sketch, "E296", {"start": v(-0.04, 3) * mm, "end": v(0.09, 3) * mm});
            skLineSegment(sketch, "E297", {"start": v(0.09, 3) * mm, "end": v(0.21, 3) * mm});
            skLineSegment(sketch, "E298", {"start": v(0.21, 3) * mm, "end": v(0.34, 3) * mm});
            skLineSegment(sketch, "E299", {"start": v(0.34, 3) * mm, "end": v(0.46, 3) * mm});
            skLineSegment(sketch, "E300", {"start": v(0.46, 3) * mm, "end": v(0.59, 3) * mm});
            skLineSegment(sketch, "E301", {"start": v(0.59, 3) * mm, "end": v(0.71, 3) * mm});
            skLineSegment(sketch, "E302", {"start": v(0.71, 3) * mm, "end": v(0.84, 3) * mm});
            skLineSegment(sketch, "E303", {"start": v(0.84, 3) * mm, "end": v(0.96, 3) * mm});
            skLineSegment(sketch, "E304", {"start": v(0.96, 3) * mm, "end": v(1.09, 3) * mm});
            skLineSegment(sketch, "E305", {"start": v(1.09, 3) * mm, "end": v(1.21, 3) * mm});
            skLineSegment(sketch, "E306", {"start": v(1.21, 3) * mm, "end": v(1.34, 3) * mm});
            skLineSegment(sketch, "E307", {"start": v(1.34, 3) * mm, "end": v(1.46, 3) * mm});
            skLineSegment(sketch, "E308", {"start": v(1.46, 3) * mm, "end": v(1.59, 3) * mm});
            skLineSegment(sketch, "E309", {"start": v(1.59, 3) * mm, "end": v(1.71, 3) * mm});
            skLineSegment(sketch, "E310", {"start": v(1.71, 3) * mm, "end": v(1.84, 3) * mm});
            skLineSegment(sketch, "E311", {"start": v(1.84, 3) * mm, "end": v(3.04, 2.96) * mm});
            skLineSegment(sketch, "E312", {"start": v(3.04, 2.96) * mm, "end": v(4.12, 2.82) * mm});
            skLineSegment(sketch, "E313", {"start": v(4.12, 2.82) * mm, "end": v(5.09, 2.6) * mm});
            skLineSegment(sketch, "E314", {"start": v(5.09, 2.6) * mm, "end": v(5.95, 2.29) * mm});
            skLineSegment(sketch, "E315", {"start": v(5.95, 2.29) * mm, "end": v(6.72, 1.9) * mm});
            skLineSegment(sketch, "E316", {"start": v(6.72, 1.9) * mm, "end": v(7.4, 1.45) * mm});
            skLineSegment(sketch, "E317", {"start": v(7.4, 1.45) * mm, "end": v(8, 0.93) * mm});
            skLineSegment(sketch, "E318", {"start": v(8, 0.93) * mm, "end": v(8.55, 0.34) * mm});
            skLineSegment(sketch, "E319", {"start": v(8.55, 0.34) * mm, "end": v(9.02, -0.3) * mm});
            skLineSegment(sketch, "E320", {"start": v(9.02, -0.3) * mm, "end": v(9.45, -1) * mm});
            skLineSegment(sketch, "E321", {"start": v(9.45, -1) * mm, "end": v(9.83, -1.73) * mm});
            skLineSegment(sketch, "E322", {"start": v(9.83, -1.73) * mm, "end": v(10.19, -2.51) * mm});
            skLineSegment(sketch, "E323", {"start": v(10.19, -2.51) * mm, "end": v(10.51, -3.33) * mm});
            skLineSegment(sketch, "E324", {"start": v(10.51, -3.33) * mm, "end": v(10.82, -4.18) * mm});
            skLineSegment(sketch, "E325", {"start": v(10.82, -4.18) * mm, "end": v(11.13, -5.05) * mm});
            skLineSegment(sketch, "E326", {"start": v(11.13, -5.05) * mm, "end": v(11.44, -5.95) * mm});
            skLineSegment(sketch, "E327", {"start": v(11.44, -5.95) * mm, "end": v(11.5, -6.1) * mm});
            skLineSegment(sketch, "E328", {"start": v(11.5, -6.1) * mm, "end": v(11.55, -6.26) * mm});
            skLineSegment(sketch, "E329", {"start": v(11.55, -6.26) * mm, "end": v(11.6, -6.41) * mm});
            skLineSegment(sketch, "E330", {"start": v(11.6, -6.41) * mm, "end": v(11.66, -6.57) * mm});
            skLineSegment(sketch, "E331", {"start": v(11.66, -6.57) * mm, "end": v(11.72, -6.72) * mm});
            skLineSegment(sketch, "E332", {"start": v(11.72, -6.72) * mm, "end": v(11.77, -6.87) * mm});
            skLineSegment(sketch, "E333", {"start": v(11.77, -6.87) * mm, "end": v(11.83, -7.03) * mm});
            skLineSegment(sketch, "E334", {"start": v(11.83, -7.03) * mm, "end": v(11.89, -7.18) * mm});
            skLineSegment(sketch, "E335", {"start": v(11.89, -7.18) * mm, "end": v(11.94, -7.33) * mm});
            skLineSegment(sketch, "E336", {"start": v(11.94, -7.33) * mm, "end": v(12, -7.49) * mm});
            skLineSegment(sketch, "E337", {"start": v(12, -7.49) * mm, "end": v(12.05, -7.64) * mm});
            skLineSegment(sketch, "E338", {"start": v(12.05, -7.64) * mm, "end": v(12.11, -7.8) * mm});
            skLineSegment(sketch, "E339", {"start": v(12.11, -7.8) * mm, "end": v(12.17, -7.95) * mm});
            skLineSegment(sketch, "E340", {"start": v(12.17, -7.95) * mm, "end": v(12.22, -8.1) * mm});
            skLineSegment(sketch, "E341", {"start": v(12.22, -8.1) * mm, "end": v(12.28, -8.26) * mm});
            skLineSegment(sketch, "E342", {"start": v(12.28, -8.26) * mm, "end": v(12.34, -8.4) * mm});
            skLineSegment(sketch, "E343", {"start": v(12.34, -8.4) * mm, "end": v(13, -9.77) * mm});
            skLineSegment(sketch, "E344", {"start": v(13, -9.77) * mm, "end": v(13.74, -11.08) * mm});
            skLineSegment(sketch, "E345", {"start": v(13.74, -11.08) * mm, "end": v(14.58, -12.32) * mm});
            skLineSegment(sketch, "E346", {"start": v(14.58, -12.32) * mm, "end": v(15.5, -13.5) * mm});
            skLineSegment(sketch, "E347", {"start": v(15.5, -13.5) * mm, "end": v(16.5, -14.62) * mm});
            skLineSegment(sketch, "E348", {"start": v(16.5, -14.62) * mm, "end": v(17.59, -15.65) * mm});
            skLineSegment(sketch, "E349", {"start": v(17.59, -15.65) * mm, "end": v(18.74, -16.61) * mm});
            skLineSegment(sketch, "E350", {"start": v(18.74, -16.61) * mm, "end": v(19.96, -17.5) * mm});
            skLineSegment(sketch, "E351", {"start": v(19.96, -17.5) * mm, "end": v(21.24, -18.28) * mm});
            skLineSegment(sketch, "E352", {"start": v(21.24, -18.28) * mm, "end": v(22.57, -18.98) * mm});
            skLineSegment(sketch, "E353", {"start": v(22.57, -18.98) * mm, "end": v(23.97, -19.58) * mm});
            skLineSegment(sketch, "E354", {"start": v(23.97, -19.58) * mm, "end": v(25.4, -20.09) * mm});
            skLineSegment(sketch, "E355", {"start": v(25.4, -20.09) * mm, "end": v(26.9, -20.49) * mm});
            skLineSegment(sketch, "E356", {"start": v(26.9, -20.49) * mm, "end": v(28.42, -20.78) * mm});
            skLineSegment(sketch, "E357", {"start": v(28.42, -20.78) * mm, "end": v(29.99, -20.95) * mm});
            skLineSegment(sketch, "E358", {"start": v(29.99, -20.95) * mm, "end": v(31.59, -21.01) * mm});
            skLineSegment(sketch, "E359", {"start": v(31.59, -21.01) * mm, "end": v(33.06, -20.96) * mm});
            skLineSegment(sketch, "E360", {"start": v(33.06, -20.96) * mm, "end": v(34.5, -20.81) * mm});
            skLineSegment(sketch, "E361", {"start": v(34.5, -20.81) * mm, "end": v(35.91, -20.57) * mm});
            skLineSegment(sketch, "E362", {"start": v(35.91, -20.57) * mm, "end": v(37.3, -20.23) * mm});
            skLineSegment(sketch, "E363", {"start": v(37.3, -20.23) * mm, "end": v(38.63, -19.8) * mm});
            skLineSegment(sketch, "E364", {"start": v(38.63, -19.8) * mm, "end": v(39.93, -19.29) * mm});
            skLineSegment(sketch, "E365", {"start": v(39.93, -19.29) * mm, "end": v(41.2, -18.69) * mm});
            skLineSegment(sketch, "E366", {"start": v(41.2, -18.69) * mm, "end": v(42.4, -18.01) * mm});
            skLineSegment(sketch, "E367", {"start": v(42.4, -18.01) * mm, "end": v(43.56, -17.26) * mm});
            skLineSegment(sketch, "E368", {"start": v(43.56, -17.26) * mm, "end": v(44.67, -16.44) * mm});
            skLineSegment(sketch, "E369", {"start": v(44.67, -16.44) * mm, "end": v(45.71, -15.55) * mm});
            skLineSegment(sketch, "E370", {"start": v(45.71, -15.55) * mm, "end": v(46.7, -14.59) * mm});
            skLineSegment(sketch, "E371", {"start": v(46.7, -14.59) * mm, "end": v(47.62, -13.57) * mm});
            skLineSegment(sketch, "E372", {"start": v(47.62, -13.57) * mm, "end": v(48.48, -12.49) * mm});
            skLineSegment(sketch, "E373", {"start": v(48.48, -12.49) * mm, "end": v(49.27, -11.35) * mm});
            skLineSegment(sketch, "E374", {"start": v(49.27, -11.35) * mm, "end": v(49.98, -10.16) * mm});
            skLineSegment(sketch, "E375", {"start": v(49.98, -10.16) * mm, "end": v(50.63, -8.94) * mm});
            skLineSegment(sketch, "E376", {"start": v(50.63, -8.94) * mm, "end": v(51.2, -7.78) * mm});
            skLineSegment(sketch, "E377", {"start": v(51.2, -7.78) * mm, "end": v(51.68, -6.66) * mm});
            skLineSegment(sketch, "E378", {"start": v(51.68, -6.66) * mm, "end": v(52.12, -5.6) * mm});
            skLineSegment(sketch, "E379", {"start": v(52.12, -5.6) * mm, "end": v(52.55, -4.61) * mm});
            skLineSegment(sketch, "E380", {"start": v(52.55, -4.61) * mm, "end": v(53, -3.68) * mm});
            skLineSegment(sketch, "E381", {"start": v(53, -3.68) * mm, "end": v(53.48, -2.82) * mm});
            skLineSegment(sketch, "E382", {"start": v(53.48, -2.82) * mm, "end": v(54.04, -2.04) * mm});
            skLineSegment(sketch, "E383", {"start": v(54.04, -2.04) * mm, "end": v(54.7, -1.33) * mm});
            skLineSegment(sketch, "E384", {"start": v(54.7, -1.33) * mm, "end": v(55.5, -0.7) * mm});
            skLineSegment(sketch, "E385", {"start": v(55.5, -0.7) * mm, "end": v(56.45, -0.16) * mm});
            skLineSegment(sketch, "E386", {"start": v(56.45, -0.16) * mm, "end": v(57.6, 0.29) * mm});
            skLineSegment(sketch, "E387", {"start": v(57.6, 0.29) * mm, "end": v(58.95, 0.64) * mm});
            skLineSegment(sketch, "E388", {"start": v(58.95, 0.64) * mm, "end": v(60.55, 0.9) * mm});
            skLineSegment(sketch, "E389", {"start": v(60.55, 0.9) * mm, "end": v(62.43, 1.06) * mm});
            skLineSegment(sketch, "E390", {"start": v(62.43, 1.06) * mm, "end": v(64.62, 1.12) * mm});
            skLineSegment(sketch, "E391", {"start": v(64.62, 1.12) * mm, "end": v(64.62, 1.5) * mm});
            skLineSegment(sketch, "E392", {"start": v(64.62, 1.5) * mm, "end": v(64.62, 1.8) * mm});
            skLineSegment(sketch, "E393", {"start": v(64.62, 1.8) * mm, "end": v(64.62, 2.06) * mm});
            skLineSegment(sketch, "E394", {"start": v(64.62, 2.06) * mm, "end": v(64.62, 2.26) * mm});
            skLineSegment(sketch, "E395", {"start": v(64.62, 2.26) * mm, "end": v(64.62, 2.44) * mm});
            skLineSegment(sketch, "E396", {"start": v(64.62, 2.44) * mm, "end": v(64.62, 2.58) * mm});
            skLineSegment(sketch, "E397", {"start": v(64.62, 2.58) * mm, "end": v(64.62, 2.7) * mm});
            skLineSegment(sketch, "E398", {"start": v(64.62, 2.7) * mm, "end": v(64.62, 2.82) * mm});
            skLineSegment(sketch, "E399", {"start": v(64.62, 2.82) * mm, "end": v(64.62, 2.94) * mm});
            skLineSegment(sketch, "E400", {"start": v(64.62, 2.94) * mm, "end": v(64.62, 3.06) * mm});
            skLineSegment(sketch, "E401", {"start": v(64.62, 3.06) * mm, "end": v(64.62, 3.2) * mm});
            skLineSegment(sketch, "E402", {"start": v(64.62, 3.2) * mm, "end": v(64.62, 3.37) * mm});
            skLineSegment(sketch, "E403", {"start": v(64.62, 3.37) * mm, "end": v(64.62, 3.57) * mm});
            skLineSegment(sketch, "E404", {"start": v(64.62, 3.57) * mm, "end": v(64.62, 3.81) * mm});
            skLineSegment(sketch, "E405", {"start": v(64.62, 3.81) * mm, "end": v(64.62, 4.11) * mm});
            skLineSegment(sketch, "E406", {"start": v(64.62, 4.11) * mm, "end": v(64.62, 4.47) * mm});
            skLineSegment(sketch, "E407", {"start": v(64.62, 4.47) * mm, "end": v(63.55, 4.48) * mm});
            skLineSegment(sketch, "E408", {"start": v(-12.52, -1.79) * mm, "end": v(-12.78, -3.52) * mm});
            skLineSegment(sketch, "E409", {"start": v(-12.78, -3.52) * mm, "end": v(-13.21, -5.2) * mm});
            skLineSegment(sketch, "E410", {"start": v(-13.21, -5.2) * mm, "end": v(-13.8, -6.8) * mm});
            skLineSegment(sketch, "E411", {"start": v(-13.8, -6.8) * mm, "end": v(-14.54, -8.33) * mm});
            skLineSegment(sketch, "E412", {"start": v(-14.54, -8.33) * mm, "end": v(-15.42, -9.77) * mm});
            skLineSegment(sketch, "E413", {"start": v(-15.42, -9.77) * mm, "end": v(-16.42, -11.12) * mm});
            skLineSegment(sketch, "E414", {"start": v(-16.42, -11.12) * mm, "end": v(-17.55, -12.36) * mm});
            skLineSegment(sketch, "E415", {"start": v(-17.55, -12.36) * mm, "end": v(-18.8, -13.49) * mm});
            skLineSegment(sketch, "E416", {"start": v(-18.8, -13.49) * mm, "end": v(-20.14, -14.5) * mm});
            skLineSegment(sketch, "E417", {"start": v(-20.14, -14.5) * mm, "end": v(-21.58, -15.37) * mm});
            skLineSegment(sketch, "E418", {"start": v(-21.58, -15.37) * mm, "end": v(-23.11, -16.1) * mm});
            skLineSegment(sketch, "E419", {"start": v(-23.11, -16.1) * mm, "end": v(-24.72, -16.7) * mm});
            skLineSegment(sketch, "E420", {"start": v(-24.72, -16.7) * mm, "end": v(-26.4, -17.13) * mm});
            skLineSegment(sketch, "E421", {"start": v(-26.4, -17.13) * mm, "end": v(-28.13, -17.4) * mm});
            skLineSegment(sketch, "E422", {"start": v(-28.13, -17.4) * mm, "end": v(-29.91, -17.49) * mm});
            skLineSegment(sketch, "E423", {"start": v(-29.91, -17.49) * mm, "end": v(-31.7, -17.4) * mm});
            skLineSegment(sketch, "E424", {"start": v(-31.7, -17.4) * mm, "end": v(-33.43, -17.13) * mm});
            skLineSegment(sketch, "E425", {"start": v(-33.43, -17.13) * mm, "end": v(-35.1, -16.7) * mm});
            skLineSegment(sketch, "E426", {"start": v(-35.1, -16.7) * mm, "end": v(-36.71, -16.1) * mm});
            skLineSegment(sketch, "E427", {"start": v(-36.71, -16.1) * mm, "end": v(-38.24, -15.37) * mm});
            skLineSegment(sketch, "E428", {"start": v(-38.24, -15.37) * mm, "end": v(-39.68, -14.5) * mm});
            skLineSegment(sketch, "E429", {"start": v(-39.68, -14.5) * mm, "end": v(-41.03, -13.49) * mm});
            skLineSegment(sketch, "E430", {"start": v(-41.03, -13.49) * mm, "end": v(-42.27, -12.36) * mm});
            skLineSegment(sketch, "E431", {"start": v(-42.27, -12.36) * mm, "end": v(-43.4, -11.12) * mm});
            skLineSegment(sketch, "E432", {"start": v(-43.4, -11.12) * mm, "end": v(-44.4, -9.77) * mm});
            skLineSegment(sketch, "E433", {"start": v(-44.4, -9.77) * mm, "end": v(-45.28, -8.33) * mm});
            skLineSegment(sketch, "E434", {"start": v(-45.28, -8.33) * mm, "end": v(-46.02, -6.8) * mm});
            skLineSegment(sketch, "E435", {"start": v(-46.02, -6.8) * mm, "end": v(-46.61, -5.2) * mm});
            skLineSegment(sketch, "E436", {"start": v(-46.61, -5.2) * mm, "end": v(-47.04, -3.52) * mm});
            skLineSegment(sketch, "E437", {"start": v(-47.04, -3.52) * mm, "end": v(-47.3, -1.79) * mm});
            skLineSegment(sketch, "E438", {"start": v(-47.3, -1.79) * mm, "end": v(-47.4, 0) * mm});
            skLineSegment(sketch, "E439", {"start": v(-47.4, 0) * mm, "end": v(-47.3, 1.79) * mm});
            skLineSegment(sketch, "E440", {"start": v(-47.3, 1.79) * mm, "end": v(-47.04, 3.52) * mm});
            skLineSegment(sketch, "E441", {"start": v(-47.04, 3.52) * mm, "end": v(-46.61, 5.2) * mm});
            skLineSegment(sketch, "E442", {"start": v(-46.61, 5.2) * mm, "end": v(-46.02, 6.8) * mm});
            skLineSegment(sketch, "E443", {"start": v(-46.02, 6.8) * mm, "end": v(-45.28, 8.33) * mm});
            skLineSegment(sketch, "E444", {"start": v(-45.28, 8.33) * mm, "end": v(-44.4, 9.77) * mm});
            skLineSegment(sketch, "E445", {"start": v(-44.4, 9.77) * mm, "end": v(-43.4, 11.12) * mm});
            skLineSegment(sketch, "E446", {"start": v(-43.4, 11.12) * mm, "end": v(-42.27, 12.36) * mm});
            skLineSegment(sketch, "E447", {"start": v(-42.27, 12.36) * mm, "end": v(-41.03, 13.49) * mm});
            skLineSegment(sketch, "E448", {"start": v(-41.03, 13.49) * mm, "end": v(-39.68, 14.5) * mm});
            skLineSegment(sketch, "E449", {"start": v(-39.68, 14.5) * mm, "end": v(-38.24, 15.37) * mm});
            skLineSegment(sketch, "E450", {"start": v(-38.24, 15.37) * mm, "end": v(-36.71, 16.1) * mm});
            skLineSegment(sketch, "E451", {"start": v(-36.71, 16.1) * mm, "end": v(-35.1, 16.7) * mm});
            skLineSegment(sketch, "E452", {"start": v(-35.1, 16.7) * mm, "end": v(-33.43, 17.13) * mm});
            skLineSegment(sketch, "E453", {"start": v(-33.43, 17.13) * mm, "end": v(-31.7, 17.4) * mm});
            skLineSegment(sketch, "E454", {"start": v(-31.7, 17.4) * mm, "end": v(-29.91, 17.49) * mm});
            skLineSegment(sketch, "E455", {"start": v(-29.91, 17.49) * mm, "end": v(-28.13, 17.4) * mm});
            skLineSegment(sketch, "E456", {"start": v(-28.13, 17.4) * mm, "end": v(-26.4, 17.13) * mm});
            skLineSegment(sketch, "E457", {"start": v(-26.4, 17.13) * mm, "end": v(-24.72, 16.7) * mm});
            skLineSegment(sketch, "E458", {"start": v(-24.72, 16.7) * mm, "end": v(-23.11, 16.1) * mm});
            skLineSegment(sketch, "E459", {"start": v(-23.11, 16.1) * mm, "end": v(-21.58, 15.37) * mm});
            skLineSegment(sketch, "E460", {"start": v(-21.58, 15.37) * mm, "end": v(-20.14, 14.5) * mm});
            skLineSegment(sketch, "E461", {"start": v(-20.14, 14.5) * mm, "end": v(-18.8, 13.49) * mm});
            skLineSegment(sketch, "E462", {"start": v(-18.8, 13.49) * mm, "end": v(-17.55, 12.36) * mm});
            skLineSegment(sketch, "E463", {"start": v(-17.55, 12.36) * mm, "end": v(-16.42, 11.12) * mm});
            skLineSegment(sketch, "E464", {"start": v(-16.42, 11.12) * mm, "end": v(-15.42, 9.77) * mm});
            skLineSegment(sketch, "E465", {"start": v(-15.42, 9.77) * mm, "end": v(-14.54, 8.33) * mm});
            skLineSegment(sketch, "E466", {"start": v(-14.54, 8.33) * mm, "end": v(-13.8, 6.8) * mm});
            skLineSegment(sketch, "E467", {"start": v(-13.8, 6.8) * mm, "end": v(-13.21, 5.2) * mm});
            skLineSegment(sketch, "E468", {"start": v(-13.21, 5.2) * mm, "end": v(-12.78, 3.52) * mm});
            skLineSegment(sketch, "E469", {"start": v(-12.78, 3.52) * mm, "end": v(-12.52, 1.79) * mm});
            skLineSegment(sketch, "E470", {"start": v(-12.52, 1.79) * mm, "end": v(-12.43, 0) * mm});
            skLineSegment(sketch, "E471", {"start": v(-12.43, 0) * mm, "end": v(-12.52, -1.79) * mm});
            skLineSegment(sketch, "E472", {"start": v(48.98, -1.79) * mm, "end": v(48.72, -3.52) * mm});
            skLineSegment(sketch, "E473", {"start": v(48.72, -3.52) * mm, "end": v(48.29, -5.2) * mm});
            skLineSegment(sketch, "E474", {"start": v(48.29, -5.2) * mm, "end": v(47.7, -6.8) * mm});
            skLineSegment(sketch, "E475", {"start": v(47.7, -6.8) * mm, "end": v(46.96, -8.33) * mm});
            skLineSegment(sketch, "E476", {"start": v(46.96, -8.33) * mm, "end": v(46.08, -9.77) * mm});
            skLineSegment(sketch, "E477", {"start": v(46.08, -9.77) * mm, "end": v(45.08, -11.12) * mm});
            skLineSegment(sketch, "E478", {"start": v(45.08, -11.12) * mm, "end": v(43.95, -12.36) * mm});
            skLineSegment(sketch, "E479", {"start": v(43.95, -12.36) * mm, "end": v(42.7, -13.49) * mm});
            skLineSegment(sketch, "E480", {"start": v(42.7, -13.49) * mm, "end": v(41.36, -14.5) * mm});
            skLineSegment(sketch, "E481", {"start": v(41.36, -14.5) * mm, "end": v(39.92, -15.37) * mm});
            skLineSegment(sketch, "E482", {"start": v(39.92, -15.37) * mm, "end": v(38.39, -16.1) * mm});
            skLineSegment(sketch, "E483", {"start": v(38.39, -16.1) * mm, "end": v(36.78, -16.7) * mm});
            skLineSegment(sketch, "E484", {"start": v(36.78, -16.7) * mm, "end": v(35.1, -17.13) * mm});
            skLineSegment(sketch, "E485", {"start": v(35.1, -17.13) * mm, "end": v(33.37, -17.4) * mm});
            skLineSegment(sketch, "E486", {"start": v(33.37, -17.4) * mm, "end": v(31.59, -17.49) * mm});
            skLineSegment(sketch, "E487", {"start": v(31.59, -17.49) * mm, "end": v(29.8, -17.4) * mm});
            skLineSegment(sketch, "E488", {"start": v(29.8, -17.4) * mm, "end": v(28.07, -17.13) * mm});
            skLineSegment(sketch, "E489", {"start": v(28.07, -17.13) * mm, "end": v(26.4, -16.7) * mm});
            skLineSegment(sketch, "E490", {"start": v(26.4, -16.7) * mm, "end": v(24.79, -16.1) * mm});
            skLineSegment(sketch, "E491", {"start": v(24.79, -16.1) * mm, "end": v(23.26, -15.37) * mm});
            skLineSegment(sketch, "E492", {"start": v(23.26, -15.37) * mm, "end": v(21.82, -14.5) * mm});
            skLineSegment(sketch, "E493", {"start": v(21.82, -14.5) * mm, "end": v(20.47, -13.49) * mm});
            skLineSegment(sketch, "E494", {"start": v(20.47, -13.49) * mm, "end": v(19.23, -12.36) * mm});
            skLineSegment(sketch, "E495", {"start": v(19.23, -12.36) * mm, "end": v(18.1, -11.12) * mm});
            skLineSegment(sketch, "E496", {"start": v(18.1, -11.12) * mm, "end": v(17.1, -9.77) * mm});
            skLineSegment(sketch, "E497", {"start": v(17.1, -9.77) * mm, "end": v(16.22, -8.33) * mm});
            skLineSegment(sketch, "E498", {"start": v(16.22, -8.33) * mm, "end": v(15.48, -6.8) * mm});
            skLineSegment(sketch, "E499", {"start": v(15.48, -6.8) * mm, "end": v(14.89, -5.2) * mm});
            skLineSegment(sketch, "E500", {"start": v(14.89, -5.2) * mm, "end": v(14.46, -3.52) * mm});
            skLineSegment(sketch, "E501", {"start": v(14.46, -3.52) * mm, "end": v(14.2, -1.79) * mm});
            skLineSegment(sketch, "E502", {"start": v(14.2, -1.79) * mm, "end": v(14.1, 0) * mm});
            skLineSegment(sketch, "E503", {"start": v(14.1, 0) * mm, "end": v(14.2, 1.79) * mm});
            skLineSegment(sketch, "E504", {"start": v(14.2, 1.79) * mm, "end": v(14.46, 3.52) * mm});
            skLineSegment(sketch, "E505", {"start": v(14.46, 3.52) * mm, "end": v(14.89, 5.2) * mm});
            skLineSegment(sketch, "E506", {"start": v(14.89, 5.2) * mm, "end": v(15.48, 6.8) * mm});
            skLineSegment(sketch, "E507", {"start": v(15.48, 6.8) * mm, "end": v(16.22, 8.33) * mm});
            skLineSegment(sketch, "E508", {"start": v(16.22, 8.33) * mm, "end": v(17.1, 9.77) * mm});
            skLineSegment(sketch, "E509", {"start": v(17.1, 9.77) * mm, "end": v(18.1, 11.12) * mm});
            skLineSegment(sketch, "E510", {"start": v(18.1, 11.12) * mm, "end": v(19.23, 12.36) * mm});
            skLineSegment(sketch, "E511", {"start": v(19.23, 12.36) * mm, "end": v(20.47, 13.49) * mm});
            skLineSegment(sketch, "E512", {"start": v(20.47, 13.49) * mm, "end": v(21.82, 14.5) * mm});
            skLineSegment(sketch, "E513", {"start": v(21.82, 14.5) * mm, "end": v(23.26, 15.37) * mm});
            skLineSegment(sketch, "E514", {"start": v(23.26, 15.37) * mm, "end": v(24.79, 16.1) * mm});
            skLineSegment(sketch, "E515", {"start": v(24.79, 16.1) * mm, "end": v(26.4, 16.7) * mm});
            skLineSegment(sketch, "E516", {"start": v(26.4, 16.7) * mm, "end": v(28.07, 17.13) * mm});
            skLineSegment(sketch, "E517", {"start": v(28.07, 17.13) * mm, "end": v(29.8, 17.4) * mm});
            skLineSegment(sketch, "E518", {"start": v(29.8, 17.4) * mm, "end": v(31.59, 17.49) * mm});
            skLineSegment(sketch, "E519", {"start": v(31.59, 17.49) * mm, "end": v(33.37, 17.4) * mm});
            skLineSegment(sketch, "E520", {"start": v(33.37, 17.4) * mm, "end": v(35.1, 17.13) * mm});
            skLineSegment(sketch, "E521", {"start": v(35.1, 17.13) * mm, "end": v(36.78, 16.7) * mm});
            skLineSegment(sketch, "E522", {"start": v(36.78, 16.7) * mm, "end": v(38.39, 16.1) * mm});
            skLineSegment(sketch, "E523", {"start": v(38.39, 16.1) * mm, "end": v(39.92, 15.37) * mm});
            skLineSegment(sketch, "E524", {"start": v(39.92, 15.37) * mm, "end": v(41.36, 14.5) * mm});
            skLineSegment(sketch, "E525", {"start": v(41.36, 14.5) * mm, "end": v(42.7, 13.49) * mm});
            skLineSegment(sketch, "E526", {"start": v(42.7, 13.49) * mm, "end": v(43.95, 12.36) * mm});
            skLineSegment(sketch, "E527", {"start": v(43.95, 12.36) * mm, "end": v(45.08, 11.12) * mm});
            skLineSegment(sketch, "E528", {"start": v(45.08, 11.12) * mm, "end": v(46.08, 9.77) * mm});
            skLineSegment(sketch, "E529", {"start": v(46.08, 9.77) * mm, "end": v(46.96, 8.33) * mm});
            skLineSegment(sketch, "E530", {"start": v(46.96, 8.33) * mm, "end": v(47.7, 6.8) * mm});
            skLineSegment(sketch, "E531", {"start": v(47.7, 6.8) * mm, "end": v(48.29, 5.2) * mm});
            skLineSegment(sketch, "E532", {"start": v(48.29, 5.2) * mm, "end": v(48.72, 3.52) * mm});
            skLineSegment(sketch, "E533", {"start": v(48.72, 3.52) * mm, "end": v(48.98, 1.79) * mm});
            skLineSegment(sketch, "E534", {"start": v(48.98, 1.79) * mm, "end": v(49.07, 0) * mm});
            skLineSegment(sketch, "E535", {"start": v(49.07, 0) * mm, "end": v(48.98, -1.79) * mm});
            skSolve(sketch);
        }
        {
            var Q0;
            Q0 = qSketchRegion(id + "F0", true);
            extrude(context, id + "F1", {"entities" : qUnion([Q0]), "depth" : 6 * mm});
        }
    });
